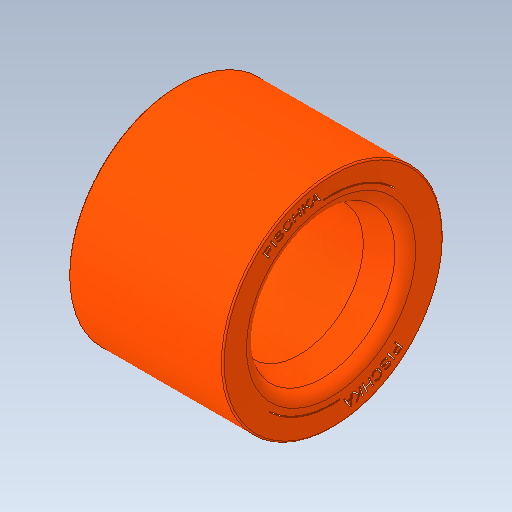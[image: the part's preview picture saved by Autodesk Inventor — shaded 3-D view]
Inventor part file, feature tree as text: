
AUTODESK INVENTOR PART (.ipt)
format: ipt  version: 2020.1 (Build 241239000, 239)  size: 904,192 bytes
history: native  units: mm
features: fillet x5, revolve x1, plane x1, emboss x1, sketch x1
ambient origin geometry x8: Origin, YZ Plane, XZ Plane, XY Plane, X Axis, Y Axis, Z Axis, Center Point
bodies: Solid1 (feature_tree)
feature tree (9):
  revolve  "Revolution1"  [1 undecoded]
  fillet  "Fillet8"  Radius=69.5mm
  fillet  "Fillet9"  Radius=63.0mm
  fillet  "Fillet10"  Radius=7.0mm
  fillet  "Fillet11"  Radius=7.0mm
  fillet  "Fillet12"  Radius=6.0mm
  plane  "Work Plane2"
  emboss  "Emboss1"
  sketch  "Sketch1"  dims[d2=90.0deg d27=46.5mm d29=69.5mm d31=63.0mm d32=7.0mm d33=7.0mm d34=6.0mm d35=55.0mm d39=80.0mm d40=1.4mm d42=5.6mm d44=19.0mm d45=19.0mm d46=56.0mm d47=0.872665mm d48=0.872665mm d49=12.5mm d50=5.0mm d54=0.5mm d55=0.1mm d56=0.0mm]
note: 1 required parameter value undecoded (feature->parameter linkage not recoverable at this tier; creation-order binding heuristic only, values carry confidence <= 0.55)
